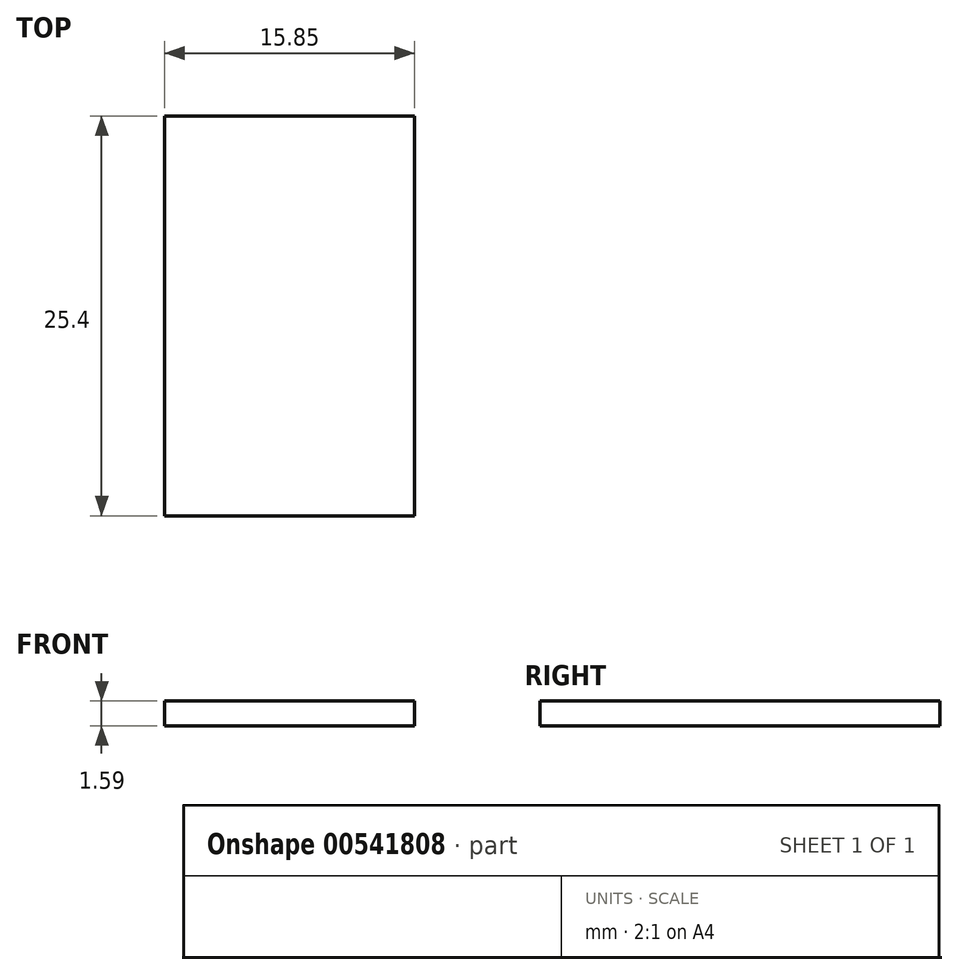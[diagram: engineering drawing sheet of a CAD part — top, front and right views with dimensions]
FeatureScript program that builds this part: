
annotation { "Feature Type Name" : "Feature", "Feature Type Description" : "" }
export const myFeature = defineFeature(function(context is Context, id is Id, definition is map)
    precondition{}
    {
        {
            var Q0;
            Q0=qCreatedBy(makeId("Top.planeOp"),FACE);
            var sketch = newSketch(context, id + "F0", { "sketchPlane" : qUnion([Q0])});
            skLineSegment(sketch, "E0", {"start": v(-23.17, 26.64) * mm, "end": v(-23.17, 1.24) * mm});
            skLineSegment(sketch, "E1", {"start": v(-23.17, 26.64) * mm, "end": v(-7.32, 26.64) * mm});
            skLineSegment(sketch, "E2", {"start": v(-7.32, 26.64) * mm, "end": v(-7.32, 1.24) * mm});
            skLineSegment(sketch, "E3", {"start": v(-7.32, 1.24) * mm, "end": v(-23.17, 1.24) * mm});
            skSolve(sketch);
        }
        {
            var Q0;
            Q0=makeQuery(id+"F0.imprint","IMPRINT",FACE,{"disambiguationData":[TD([[makeQuery(id+"F0.imprint","IMPRINT",EDGE,{"derivedFrom":sQuery(id+"F0.wireOp",EDGE,"E0")}),1.0]])]});
            extrude(context, id + "F1", {"entities" : qUnion([Q0]), "depth" : 1.59 * mm, "offsetDistance" : 25.4 * mm});
        }
    });
